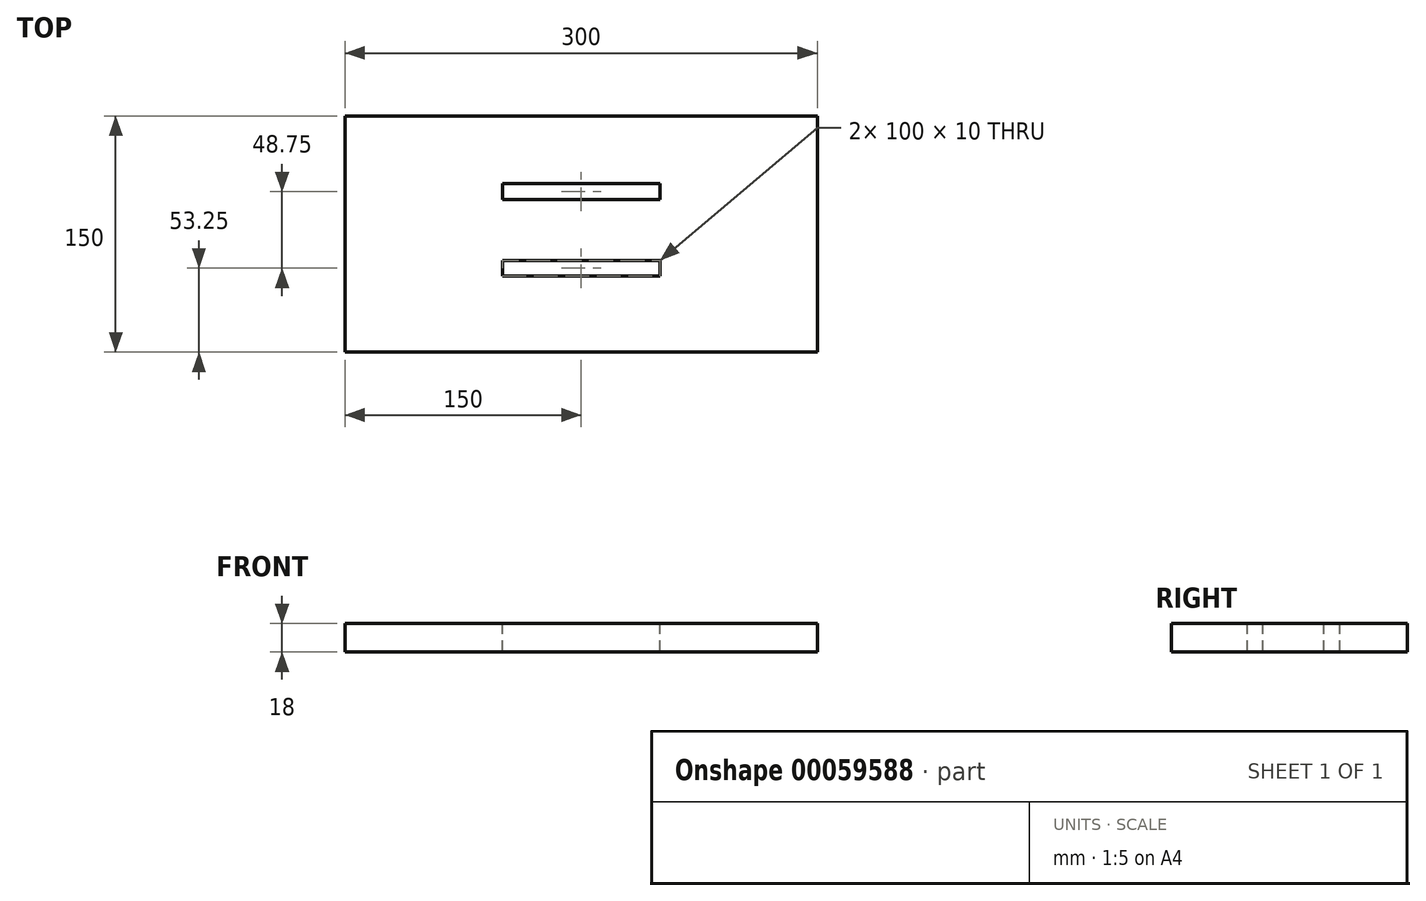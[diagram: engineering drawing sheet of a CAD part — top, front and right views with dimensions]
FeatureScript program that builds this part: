
annotation { "Feature Type Name" : "Feature", "Feature Type Description" : "" }
export const myFeature = defineFeature(function(context is Context, id is Id, definition is map)
    precondition{}
    {
        {
            var Q0;
            Q0=qCreatedBy(makeId("Top.planeOp"),FACE);
            var sketch = newSketch(context, id + "F0", { "sketchPlane" : qUnion([Q0])});
            skLineSegment(sketch, "E0.rect.bottom", {"start": v(-150, 75) * mm, "end": v(150, 75) * mm});
            skLineSegment(sketch, "E0.rect.top", {"start": v(-150, -75) * mm, "end": v(150, -75) * mm});
            skLineSegment(sketch, "E0.rect.left", {"start": v(-150, 75) * mm, "end": v(-150, -75) * mm});
            skLineSegment(sketch, "E0.rect.right", {"start": v(150, 75) * mm, "end": v(150, -75) * mm});
            skPoint(sketch, "E0.rect.middle", {"position": v(0, 0) * mm});
            skSolve(sketch);
        }
        {
            var Q0;
            Q0 = qSketchRegion(id + "F0", true);
            extrude(context, id + "F1", {"entities" : qUnion([Q0]), "depth" : 18 * mm});
        }
        {
            var Q0;
            Q0=makeQuery(id+"F1.opExtrude","CAP_FACE",FACE,{"disambiguationData":[OSD([sQuery(id+"F0.wireOp",EDGE,"E0.rect.bottom"),sQuery(id+"F0.wireOp",EDGE,"E0.rect.top"),sQuery(id+"F0.wireOp",EDGE,"E0.rect.left"),sQuery(id+"F0.wireOp",EDGE,"E0.rect.right")])],"isStart":false});
            var sketch = newSketch(context, id + "F2", { "sketchPlane" : qUnion([Q0])});
            skLineSegment(sketch, "E1.MirrorCS", {"start": v(50, -26.75) * mm, "end": v(50, -16.75) * mm});
            skLineSegment(sketch, "E2.MirrorCS", {"start": v(-50, -26.75) * mm, "end": v(-50, -16.75) * mm});
            skLineSegment(sketch, "E3.MirrorCS", {"start": v(-50, -26.75) * mm, "end": v(50, -26.75) * mm});
            skLineSegment(sketch, "E4.MirrorCS", {"start": v(-50, -16.75) * mm, "end": v(50, -16.75) * mm});
            skPoint(sketch, "E5.MirrorP", {"position": v(0, -21.75) * mm});
            skLineSegment(sketch, "E6.MirrorCS", {"start": v(50, 22) * mm, "end": v(50, 32) * mm});
            skLineSegment(sketch, "E7.MirrorCS", {"start": v(-50, 22) * mm, "end": v(-50, 32) * mm});
            skLineSegment(sketch, "E8.MirrorCS", {"start": v(-50, 22) * mm, "end": v(50, 22) * mm});
            skLineSegment(sketch, "E9.MirrorCS", {"start": v(-50, 32) * mm, "end": v(50, 32) * mm});
            skPoint(sketch, "E10.MirrorP", {"position": v(0, 22.53) * mm});
            skSolve(sketch);
        }
        {
            var Q0;
            Q0 = qSketchRegion(id + "F2", true);
            extrude(context, id + "F3", {"entities" : qUnion([Q0]), "operationType" : NewBodyOperationType.REMOVE, "oppositeDirection" : true, "depth" : 18 * mm});
        }
    });
